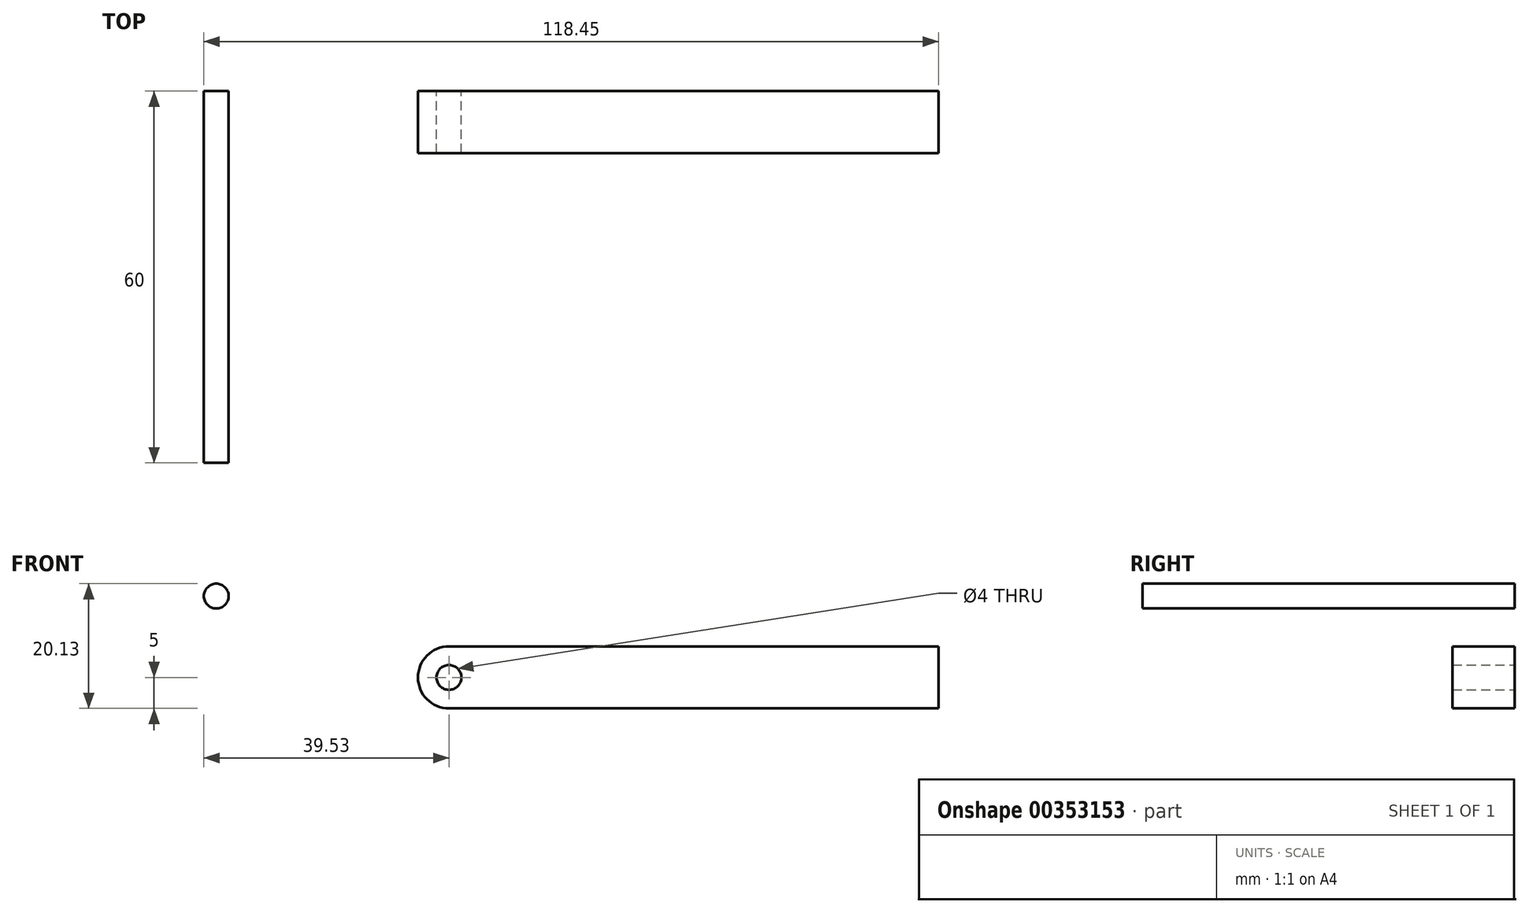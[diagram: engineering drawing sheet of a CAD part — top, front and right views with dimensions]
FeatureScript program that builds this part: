
annotation { "Feature Type Name" : "Feature", "Feature Type Description" : "" }
export const myFeature = defineFeature(function(context is Context, id is Id, definition is map)
    precondition{}
    {
        {
            var Q0;
            Q0=qCreatedBy(makeId("Front.planeOp"),FACE);
            var sketch = newSketch(context, id + "F0", { "sketchPlane" : qUnion([Q0])});
            skLineSegment(sketch, "E0.bottom", {"start": v(5, 0) * mm, "end": v(83.92, 0) * mm});
            skLineSegment(sketch, "E0.top", {"start": v(5, 10) * mm, "end": v(83.92, 10) * mm});
            skLineSegment(sketch, "E0.left", {"start": v(0, 5) * mm, "end": v(0, 5) * mm});
            skLineSegment(sketch, "E0.right", {"start": v(83.92, 0) * mm, "end": v(83.92, 10) * mm});
            skPoint(sketch, "E1.visualSharp", {"position": v(0, 10) * mm});
            skArc(sketch, "E1.filletArc", {"start": v(5, 10) * mm, "mid": v(1.46, 8.54) * mm, "end": v(0, 5) * mm});
            skPoint(sketch, "E2.visualSharp", {"position": v(0, 0) * mm});
            skArc(sketch, "E2.filletArc", {"start": v(0, 5) * mm, "mid": v(1.46, 1.46) * mm, "end": v(5, 0) * mm});
            skCircle(sketch, "E3", {"center": v(5, 5) * mm, "radius": 2 * mm});
            skSolve(sketch);
        }
        {
            var Q0;
            Q0 = qSketchRegion(id + "F0", true);
            extrude(context, id + "F1", {"entities" : qUnion([Q0]), "depth" : 10 * mm});
        }
        {
            var Q0;
            Q0=qCreatedBy(makeId("Front.planeOp"),FACE);
            var sketch = newSketch(context, id + "F2", { "sketchPlane" : qUnion([Q0])});
            skCircle(sketch, "E4", {"center": v(-32.53, 18.13) * mm, "radius": 2 * mm});
            skSolve(sketch);
        }
        {
            var Q0;
            Q0 = qSketchRegion(id + "F2", true);
            extrude(context, id + "F3", {"entities" : qUnion([Q0]), "depth" : 60 * mm});
        }
    });
